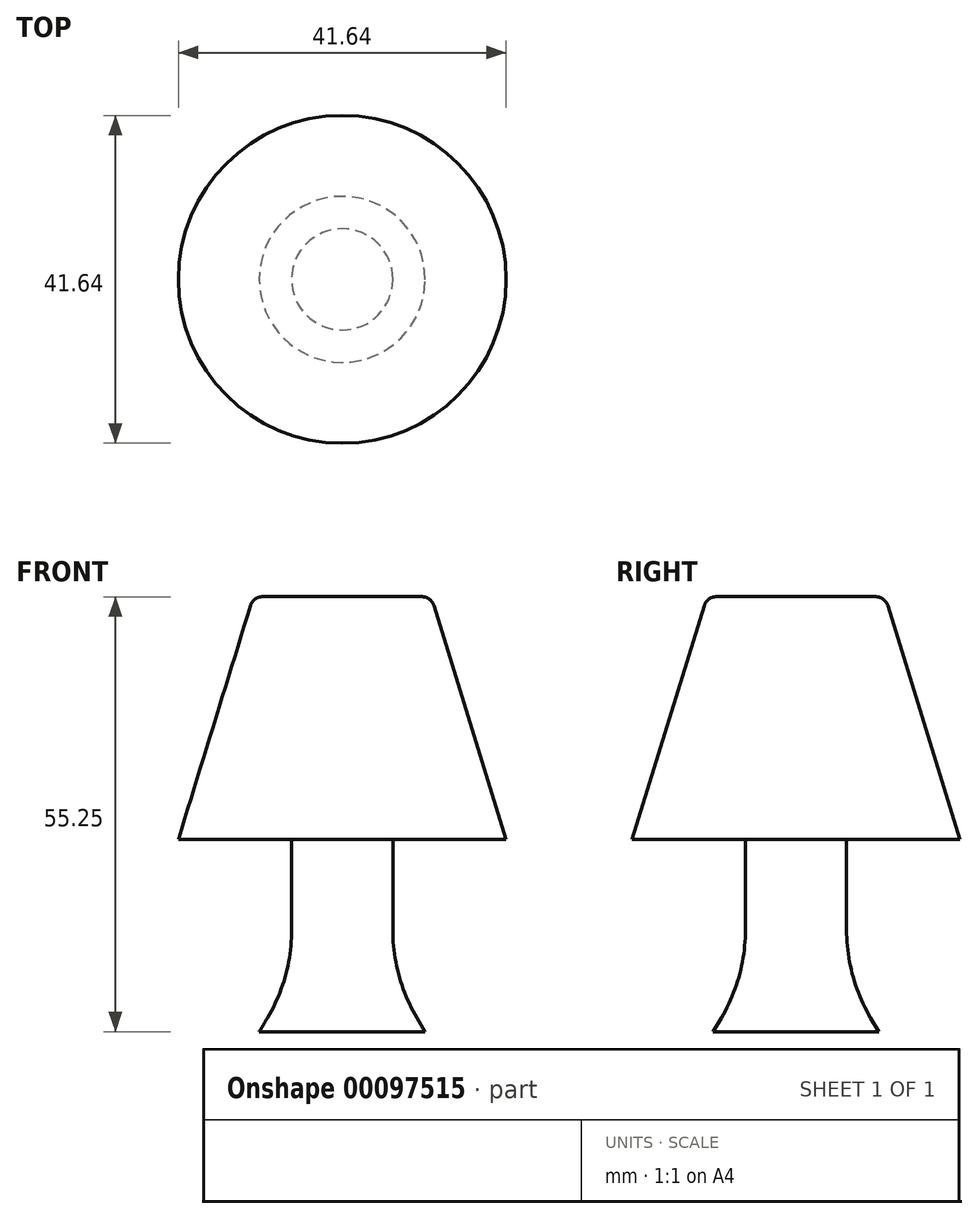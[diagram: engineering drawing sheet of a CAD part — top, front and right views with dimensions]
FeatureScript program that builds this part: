
annotation { "Feature Type Name" : "Feature", "Feature Type Description" : "" }
export const myFeature = defineFeature(function(context is Context, id is Id, definition is map)
    precondition{}
    {
        {
            var Q0;
            Q0=qCreatedBy(makeId("Front.planeOp"),FACE);
            var sketch = newSketch(context, id + "F0", { "sketchPlane" : qUnion([Q0])});
            skLineSegment(sketch, "E0", {"start": v(-41.7, 43.83) * mm, "end": v(-30.4, 43.83) * mm});
            skLineSegment(sketch, "E1", {"start": v(-30.4, 43.83) * mm, "end": v(-20.9, 13) * mm});
            skLineSegment(sketch, "E2", {"start": v(-20.9, 13) * mm, "end": v(-35.28, 13) * mm});
            skLineSegment(sketch, "E3", {"start": v(-35.28, 13) * mm, "end": v(-35.28, -4.48) * mm});
            skLineSegment(sketch, "E4", {"start": v(-35.28, -4.48) * mm, "end": v(-31.17, -11.42) * mm});
            skLineSegment(sketch, "E5", {"start": v(-31.17, -11.42) * mm, "end": v(-41.7, -11.42) * mm});
            skLineSegment(sketch, "E6", {"start": v(-41.7, -11.42) * mm, "end": v(-41.7, 43.83) * mm});
            skSolve(sketch);
        }
        {
            var Q0;
            Q0=makeQuery(id+"F0.imprint","IMPRINT",FACE,{"disambiguationData":[TD([[makeQuery(id+"F0.imprint","IMPRINT",EDGE,{"derivedFrom":sQuery(id+"F0.wireOp",EDGE,"E0")}),-1.0]])]});
            var Q1;
            Q1=sQuery(id+"F0.wireOp",EDGE,"E6");
            revolve(context, id + "F1", {"entities" : qUnion([Q0]), "axis" : qUnion([Q1]), "revolveType" : RevolveType.FULL});
        }
        {
            var Q0;
            Q0=makeQuery(id+"F1.opRevolve","SWEPT_EDGE",EDGE,{"disambiguationData":[OSD([sQuery(id+"F0.wireOp",EDGE,"E0"),sQuery(id+"F0.wireOp",EDGE,"E1")])]});
            fillet(context, id + "F2", {"entities" : qUnion([Q0]), "radius" : 1.6 * mm, "tangentPropagation" : true, "allowEdgeOverflow" : false});
        }
        {
            var Q0;
            Q0=makeQuery(id+"F1.opRevolve","SWEPT_EDGE",EDGE,{"disambiguationData":[OSD([sQuery(id+"F0.wireOp",EDGE,"E3"),sQuery(id+"F0.wireOp",EDGE,"E4")])]});
            fillet(context, id + "F3", {"entities" : qUnion([Q0]), "radius" : 21.87 * mm, "tangentPropagation" : true, "allowEdgeOverflow" : false});
        }
    });
